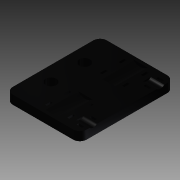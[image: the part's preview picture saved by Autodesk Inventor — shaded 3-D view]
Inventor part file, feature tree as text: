
AUTODESK INVENTOR PART (.ipt)
format: ipt  version: 2013 (Build 170138000, 138)  size: 212,480 bytes
history: native  units: mm
features: extrude x4, sketch x4, mirror x2, fillet x1
ambient origin geometry x8: Origin, YZ Plane, XZ Plane, XY Plane, X Axis, Y Axis, Z Axis, Center Point
bodies: Solid1 (feature_tree)
feature tree (11):
  extrude  "Extrusion1"  Depth=11.0mm
  extrude  "Extrusion2"  Depth=8.0mm
  mirror  "Mirror1"
  fillet  "Fillet1"  Radius=24.0mm
  extrude  "Extrusion3"  Depth=15.0mm
  extrude  "Extrusion4"  Depth=22.5mm
  mirror  "Mirror2"
  sketch  "Sketch1"  dims[d0=70.0mm d2=11.0mm]
  sketch  "Sketch2"  dims[d3=25.0mm d4=8.0mm d5=24.0mm]
  sketch  "Sketch3"  dims[d6=45.0deg d7=15.0mm]
  sketch  "Sketch4"  dims[d9=2.5mm d10=22.5mm d11=22.5mm d12=55.0mm d13=10.0mm d15=45.0deg d16=8.0mm d17=10.0mm d18=6.477mm d19=0.0mm d20=4.0mm d22=1.5mm d23=8.0mm d24=15.0mm d25=5.0mm d26=6.477mm d27=0.0mm d28=5.0mm d29=15.0mm d31=10.0mm d32=0.0mm d33=8.0mm d35=10.0mm d36=0.0mm]
